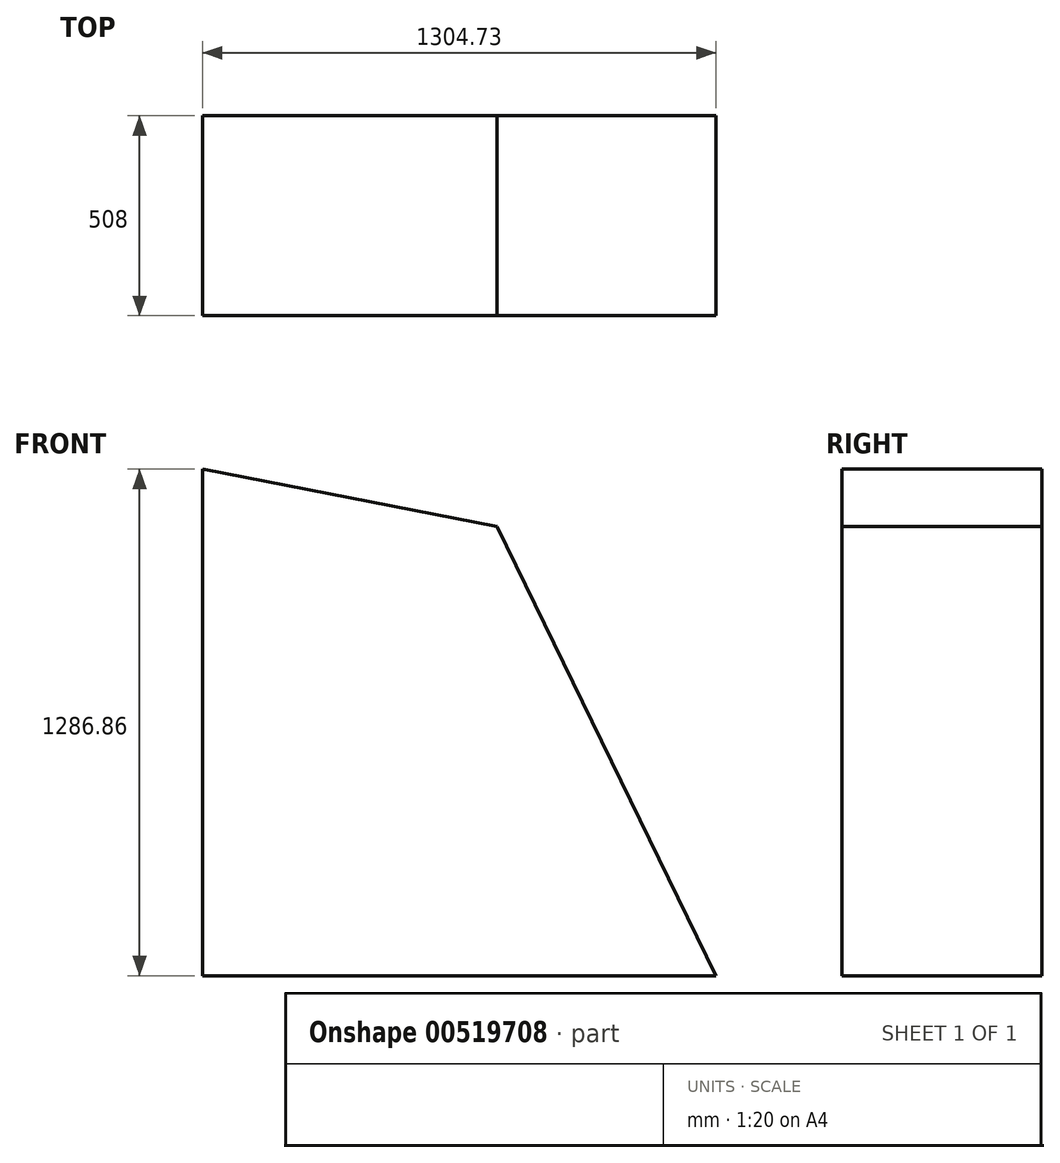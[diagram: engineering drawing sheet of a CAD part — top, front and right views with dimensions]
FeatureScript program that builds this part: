
annotation { "Feature Type Name" : "Feature", "Feature Type Description" : "" }
export const myFeature = defineFeature(function(context is Context, id is Id, definition is map)
    precondition{}
    {
        {
            var Q0;
            Q0=qCreatedBy(makeId("Front.planeOp"),FACE);
            var sketch = newSketch(context, id + "F0", { "sketchPlane" : qUnion([Q0])});
            skLineSegment(sketch, "E0", {"start": v(0, 0) * mm, "end": v(75.2, 0) * mm});
            skLineSegment(sketch, "E1", {"start": v(75.2, 0) * mm, "end": v(-481.53, 1141.47) * mm});
            skLineSegment(sketch, "E2", {"start": v(-1229.53, 0) * mm, "end": v(0, 0) * mm});
            skLineSegment(sketch, "E3", {"start": v(-481.53, 1141.47) * mm, "end": v(-1229.53, 1286.86) * mm});
            skLineSegment(sketch, "E4", {"start": v(-1229.53, 1286.86) * mm, "end": v(-1229.53, 0) * mm});
            skSolve(sketch);
        }
        {
            var Q0;
            Q0=makeQuery(id+"F0.imprint","IMPRINT",FACE,{"disambiguationData":[TD([[makeQuery(id+"F0.imprint","IMPRINT",EDGE,{"derivedFrom":sQuery(id+"F0.wireOp",EDGE,"E0")}),1.0]])]});
            extrude(context, id + "F1", {"entities" : qUnion([Q0]), "depth" : 508 * mm, "offsetDistance" : 25.4 * mm});
        }
    });
